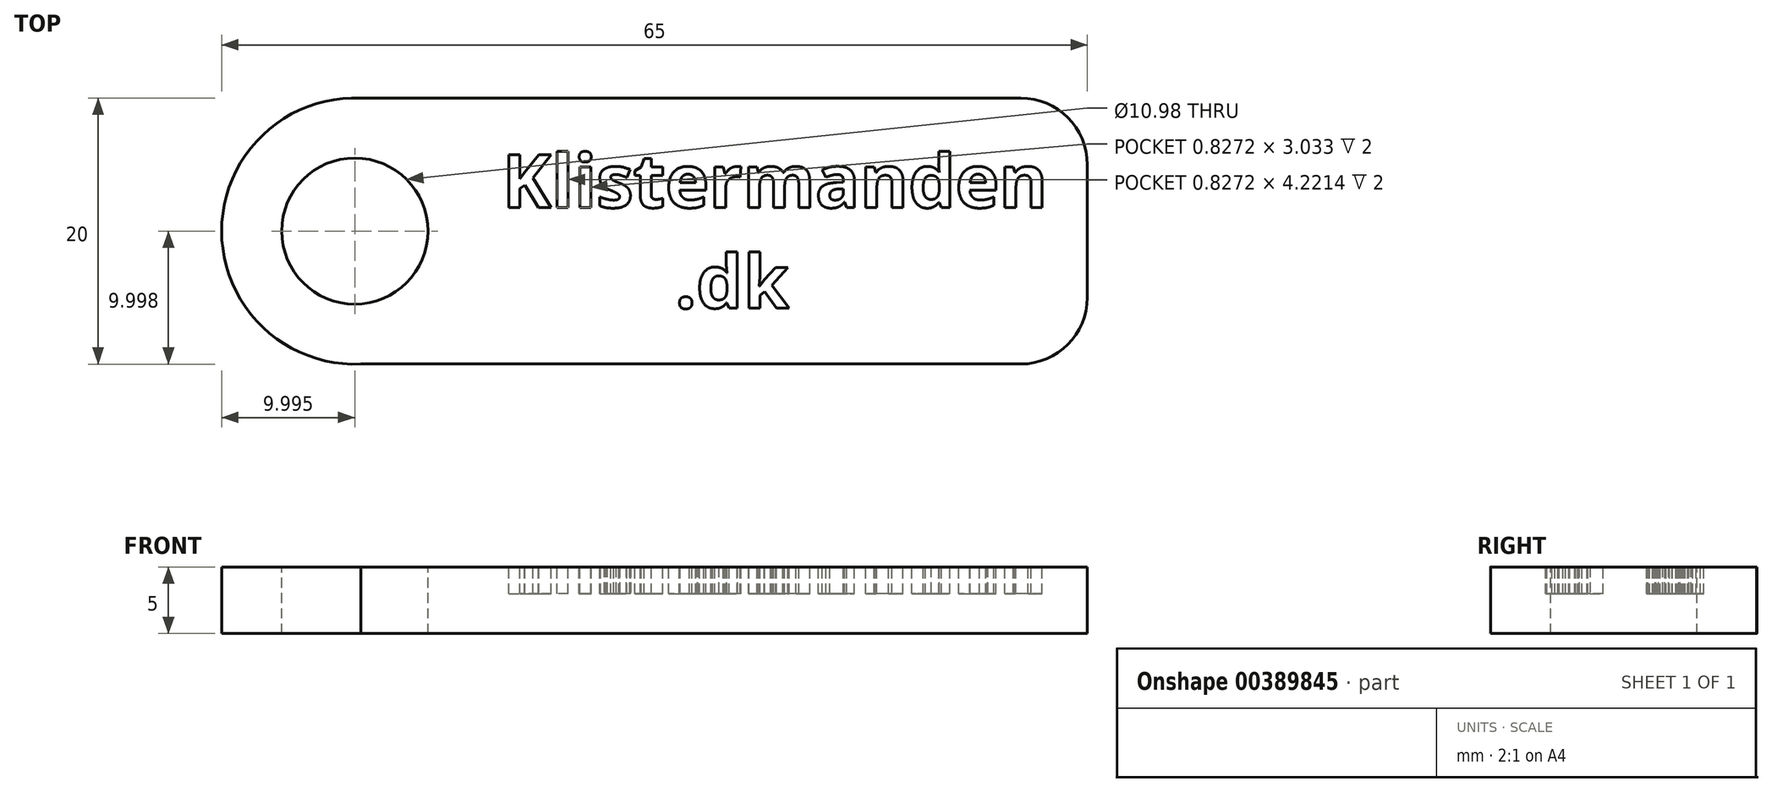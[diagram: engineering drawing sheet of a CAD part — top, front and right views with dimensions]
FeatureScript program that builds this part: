
annotation { "Feature Type Name" : "Feature", "Feature Type Description" : "" }
export const myFeature = defineFeature(function(context is Context, id is Id, definition is map)
    precondition{}
    {
        {
            var Q0;
            Q0=qCreatedBy(makeId("Top.planeOp"),FACE);
            var sketch = newSketch(context, id + "F0", { "sketchPlane" : qUnion([Q0])});
            skLineSegment(sketch, "E0.bottom", {"start": v(-9.25, 35) * mm, "end": v(40.75, 35) * mm});
            skLineSegment(sketch, "E0.top", {"start": v(-9.25, 15.02) * mm, "end": v(40.75, 15.02) * mm});
            skLineSegment(sketch, "E0.left", {"start": v(-9.25, 35) * mm, "end": v(-9.25, 15.02) * mm});
            skLineSegment(sketch, "E0.right", {"start": v(45.75, 30) * mm, "end": v(45.75, 20.02) * mm});
            skCircle(sketch, "E1", {"center": v(-9.25, 25) * mm, "radius": 10 * mm});
            skCircle(sketch, "E2", {"center": v(-9.25, 25) * mm, "radius": 5.49 * mm});
            skPoint(sketch, "E3.visualSharp", {"position": v(45.75, 35) * mm});
            skArc(sketch, "E3.filletArc", {"start": v(45.75, 30) * mm, "mid": v(44.28, 33.53) * mm, "end": v(40.75, 35) * mm});
            skPoint(sketch, "E4.visualSharp", {"position": v(45.75, 15.02) * mm});
            skArc(sketch, "E4.filletArc", {"start": v(40.75, 15.02) * mm, "mid": v(44.28, 16.48) * mm, "end": v(45.75, 20.02) * mm});
            skSolve(sketch);
        }
        {
            var Q0;
            Q0 = qSketchRegion(id + "F0", true);
            extrude(context, id + "F1", {"entities" : qUnion([Q0]), "oppositeDirection" : true, "depth" : 5 * mm});
        }
        {
            var Q0;
            Q0=qCreatedBy(makeId("Top.planeOp"),FACE);
            var sketch = newSketch(context, id + "F2", { "sketchPlane" : qUnion([Q0])});
            skText(sketch, "E5", { "text": "Klistermanden\n         .dk", "fontName": "OpenSans-Bold.ttf"});
            const initialGuessF2  = {"E5": [0.00181, 0.02678, 1, 0, 0.004]};
            skSetInitialGuess(sketch, initialGuessF2);
            skSolve(sketch);
        }
        {
            var Q0;
            Q0 = qSketchRegion(id + "F2", true);
            extrude(context, id + "F3", {"entities" : qUnion([Q0]), "operationType" : NewBodyOperationType.REMOVE, "oppositeDirection" : true, "depth" : 2 * mm});
        }
    });
